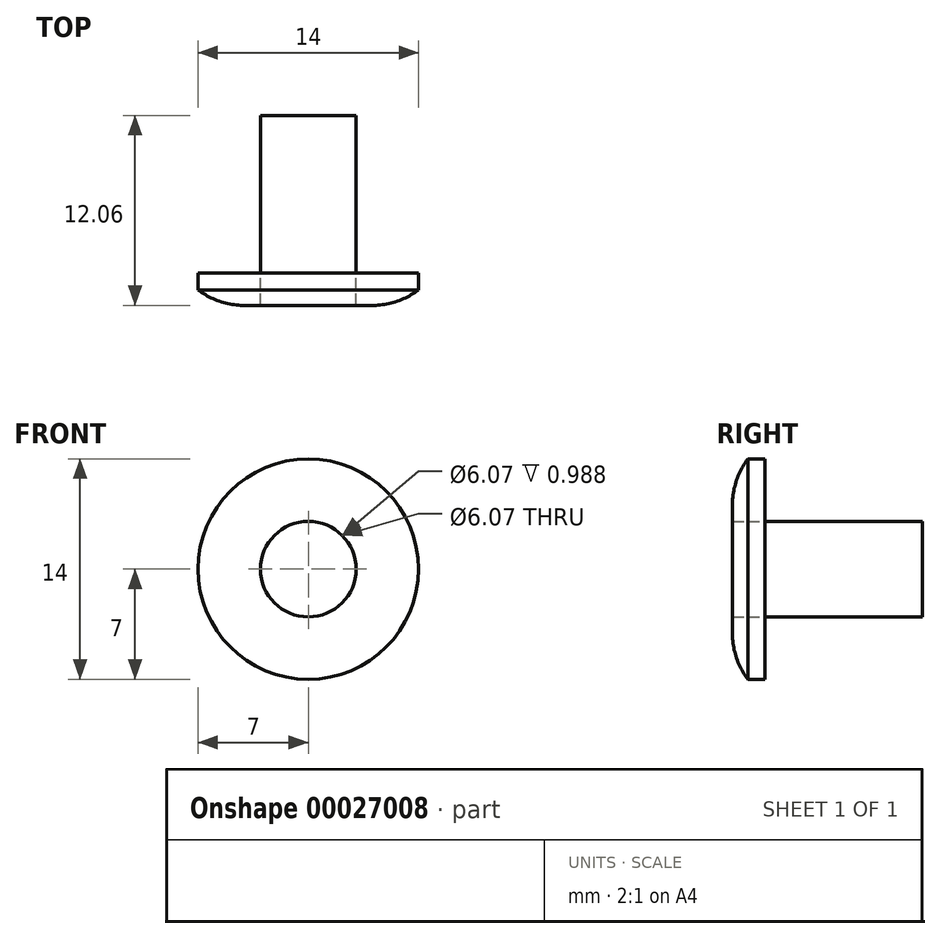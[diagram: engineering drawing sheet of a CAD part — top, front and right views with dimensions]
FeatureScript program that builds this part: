
annotation { "Feature Type Name" : "Feature", "Feature Type Description" : "" }
export const myFeature = defineFeature(function(context is Context, id is Id, definition is map)
    precondition{}
    {
        {
            var Q0;
            Q0=qCreatedBy(makeId("Front.planeOp"),FACE);
            var sketch = newSketch(context, id + "F0", { "sketchPlane" : qUnion([Q0])});
            skCircle(sketch, "E0", {"center": v(0, 0) * mm, "radius": 3.04 * mm});
            skSolve(sketch);
        }
        {
            var Q0;
            Q0=makeQuery(id+"F0.imprint","IMPRINT",FACE,{"disambiguationData":[TD([[makeQuery(id+"F0.imprint","IMPRINT",EDGE,{"derivedFrom":sQuery(id+"F0.wireOp",EDGE,"E0")}),1.0]])]});
            extrude(context, id + "F1", {"entities" : qUnion([Q0]), "depth" : 10 * mm});
        }
        {
            var Q0;
            Q0=makeQuery(id+"F1.opExtrude","CAP_FACE",FACE,{"disambiguationData":[OSD([sQuery(id+"F0.wireOp",EDGE,"E0")])],"isStart":false});
            var sketch = newSketch(context, id + "F2", { "sketchPlane" : qUnion([Q0])});
            skCircle(sketch, "E1", {"center": v(0, 0) * mm, "radius": 7 * mm});
            skLineSegment(sketch, "E2", {"start": v(0, 0) * mm, "end": v(7, 0) * mm});
            skSolve(sketch);
        }
        {
            var Q0;
            Q0=makeQuery(id+"F2.imprint","IMPRINT",FACE,{"disambiguationData":[TD([[makeQuery(id+"F2.imprint","IMPRINT",EDGE,{"derivedFrom":sQuery(id+"F2.wireOp",EDGE,"E1")}),1.0]])]});
            extrude(context, id + "F3", {"entities" : qUnion([Q0]), "depth" : 1.07 * mm});
        }
        {
            var Q0;
            Q0=makeQuery(id+"F1.opExtrude","CAP_FACE",FACE,{"disambiguationData":[OSD([sQuery(id+"F0.wireOp",EDGE,"E0")])],"isStart":false});
            var Q1;
            Q1=makeQuery(id+"F3.opExtrude","CAP_FACE",FACE,{"disambiguationData":[OSD([sQuery(id+"F0.wireOp",EDGE,"E0"),sQuery(id+"F2.wireOp",EDGE,"E1")])],"isStart":false});
            extrude(context, id + "F4", {"entities" : qUnion([Q0]), "endBound" : BoundingType.UP_TO_SURFACE, "endBoundEntityFace" : qUnion([Q1]), "depth" : 1.04 * mm});
        }
        {
            var Q0;
            Q0=makeQuery(id+"F4.opExtrude","CAP_FACE",FACE,{"disambiguationData":[OSD([sQuery(id+"F0.wireOp",EDGE,"E0")])],"isStart":false});
            var Q1;
            Q1=makeQuery(id+"F3.opExtrude","CAP_FACE",FACE,{"disambiguationData":[OSD([sQuery(id+"F0.wireOp",EDGE,"E0"),sQuery(id+"F2.wireOp",EDGE,"E1")])],"isStart":false});
            extrude(context, id + "F5", {"entities" : qUnion([Q0, Q1]), "depth" : 0.99 * mm});
        }
        {
            var Q0;
            Q0=makeQuery(id+"F5.opExtrude","CAP_EDGE",EDGE,{"disambiguationData":[OSD([sQuery(id+"F2.wireOp",EDGE,"E1")])],"isStart":false});
            fillet(context, id + "F6", {"entities" : qUnion([Q0]), "radius" : 5 * mm, "tangentPropagation" : true, "allowEdgeOverflow" : false});
        }
    });
